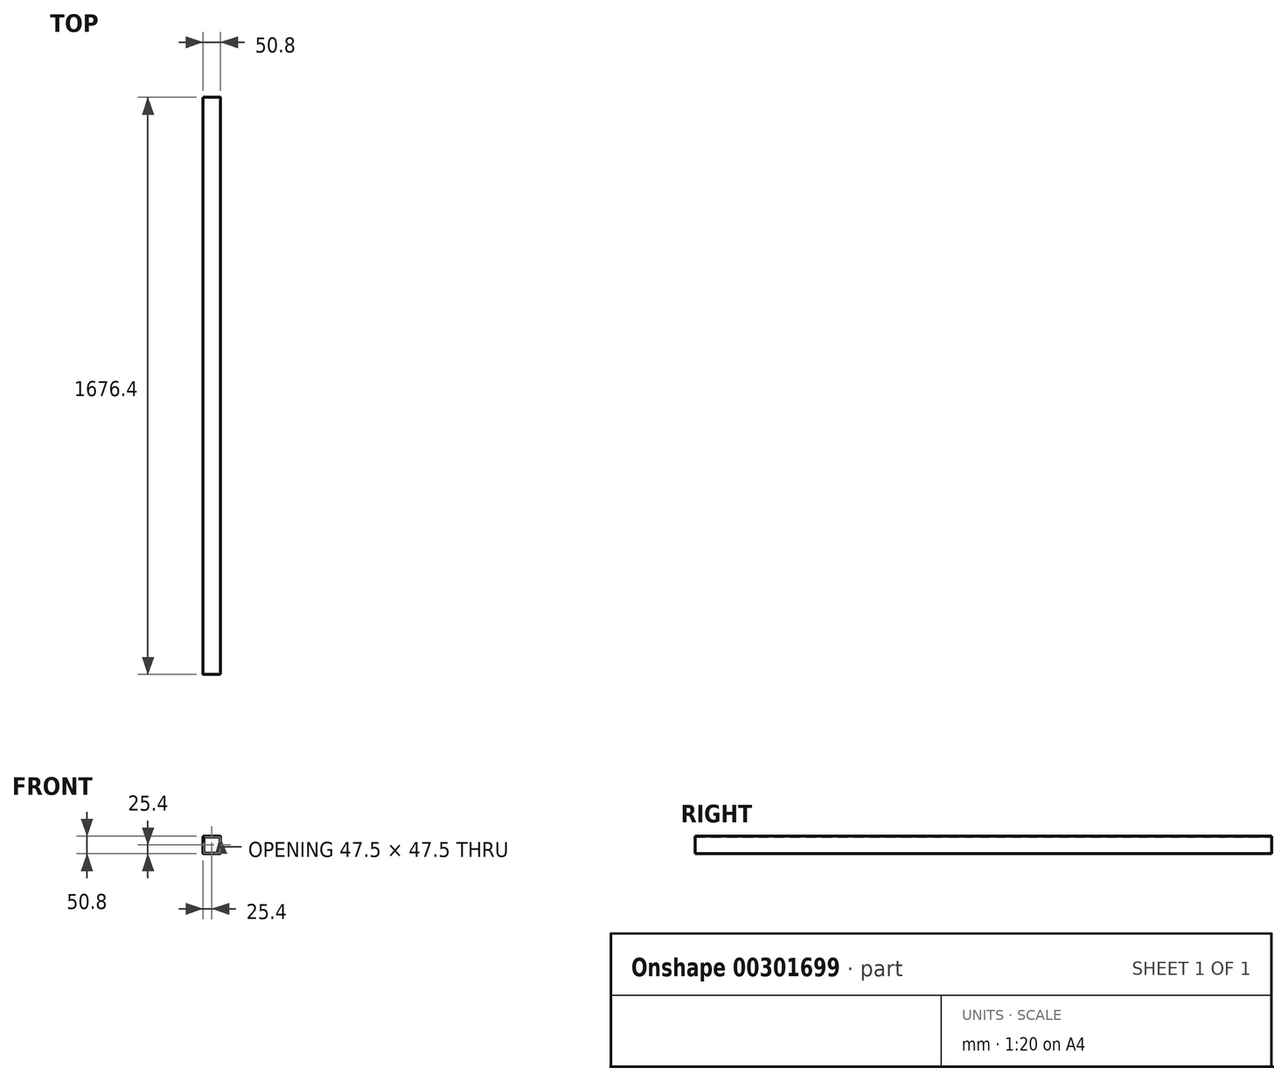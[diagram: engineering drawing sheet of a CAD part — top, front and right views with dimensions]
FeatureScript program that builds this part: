
annotation { "Feature Type Name" : "Feature", "Feature Type Description" : "" }
export const myFeature = defineFeature(function(context is Context, id is Id, definition is map)
    precondition{}
    {
        {
            var Q0;
            Q0=qCreatedBy(makeId("Front.planeOp"),FACE);
            var sketch = newSketch(context, id + "F0", { "sketchPlane" : qUnion([Q0])});
            skLineSegment(sketch, "E0.bottom", {"start": v(23.75, -25.4) * mm, "end": v(-23.75, -25.4) * mm});
            skLineSegment(sketch, "E0.top", {"start": v(23.75, 25.4) * mm, "end": v(-23.75, 25.4) * mm});
            skLineSegment(sketch, "E0.left", {"start": v(25.4, -23.75) * mm, "end": v(25.4, 23.75) * mm});
            skLineSegment(sketch, "E0.right", {"start": v(-25.4, -23.75) * mm, "end": v(-25.4, 23.75) * mm});
            skPoint(sketch, "E0.middle", {"position": v(0, 0) * mm});
            skLineSegment(sketch, "E1.0", {"start": v(22.1, 23.75) * mm, "end": v(-22.1, 23.75) * mm});
            skLineSegment(sketch, "E1.1", {"start": v(23.75, -22.1) * mm, "end": v(23.75, 22.1) * mm});
            skLineSegment(sketch, "E1.2", {"start": v(22.1, -23.75) * mm, "end": v(-22.1, -23.75) * mm});
            skLineSegment(sketch, "E1.3", {"start": v(-23.75, -22.1) * mm, "end": v(-23.75, 22.1) * mm});
            skPoint(sketch, "E2.visualSharp", {"position": v(-23.75, 23.75) * mm});
            skArc(sketch, "E2.filletArc", {"start": v(-22.1, 23.75) * mm, "mid": v(-23.27, 23.27) * mm, "end": v(-23.75, 22.1) * mm});
            skPoint(sketch, "E3.visualSharp", {"position": v(23.75, 23.75) * mm});
            skArc(sketch, "E3.filletArc", {"start": v(23.75, 22.1) * mm, "mid": v(23.27, 23.27) * mm, "end": v(22.1, 23.75) * mm});
            skPoint(sketch, "E4.visualSharp", {"position": v(23.75, -23.75) * mm});
            skArc(sketch, "E4.filletArc", {"start": v(22.1, -23.75) * mm, "mid": v(23.27, -23.27) * mm, "end": v(23.75, -22.1) * mm});
            skPoint(sketch, "E5.visualSharp", {"position": v(-23.75, -23.75) * mm});
            skArc(sketch, "E5.filletArc", {"start": v(-23.75, -22.1) * mm, "mid": v(-23.27, -23.27) * mm, "end": v(-22.1, -23.75) * mm});
            skPoint(sketch, "E6.visualSharp", {"position": v(-25.4, 25.4) * mm});
            skArc(sketch, "E6.filletArc", {"start": v(-23.75, 25.4) * mm, "mid": v(-24.92, 24.92) * mm, "end": v(-25.4, 23.75) * mm});
            skPoint(sketch, "E7.visualSharp", {"position": v(25.4, 25.4) * mm});
            skArc(sketch, "E7.filletArc", {"start": v(25.4, 23.75) * mm, "mid": v(24.92, 24.92) * mm, "end": v(23.75, 25.4) * mm});
            skPoint(sketch, "E8.visualSharp", {"position": v(25.4, -25.4) * mm});
            skArc(sketch, "E8.filletArc", {"start": v(23.75, -25.4) * mm, "mid": v(24.92, -24.92) * mm, "end": v(25.4, -23.75) * mm});
            skPoint(sketch, "E9.visualSharp", {"position": v(-25.4, -25.4) * mm});
            skArc(sketch, "E9.filletArc", {"start": v(-25.4, -23.75) * mm, "mid": v(-24.92, -24.92) * mm, "end": v(-23.75, -25.4) * mm});
            skSolve(sketch);
        }
        {
            var Q0;
            Q0=makeQuery(id+"F0.imprint","IMPRINT",FACE,{"disambiguationData":[TD([[makeQuery(id+"F0.imprint","IMPRINT",EDGE,{"derivedFrom":sQuery(id+"F0.wireOp",EDGE,"E0.bottom")}),-1.0]])]});
            var Q1;
            Q1=sQuery(id+"F0.wireOp",EDGE,"E0.left");
            var Q2;
            Q2=sQuery(id+"F0.wireOp",EDGE,"E0.right");
            var Q3;
            Q3=sQuery(id+"F0.wireOp",EDGE,"E0.top");
            var Q4;
            Q4=sQuery(id+"F0.wireOp",EDGE,"E0.bottom");
            var Q5;
            Q5=sQuery(id+"F0.wireOp",EDGE,"E1.3");
            var Q6;
            Q6=sQuery(id+"F0.wireOp",EDGE,"E1.1");
            var Q7;
            Q7=sQuery(id+"F0.wireOp",EDGE,"E1.2");
            var Q8;
            Q8=sQuery(id+"F0.wireOp",EDGE,"E1.0");
            extrude(context, id + "F1", {"entities" : qUnion([Q0]), "surfaceEntities" : qUnion([Q1, Q2, Q3, Q4, Q5, Q6, Q7, Q8]), "depth" : 1676.4 * mm});
        }
    });
